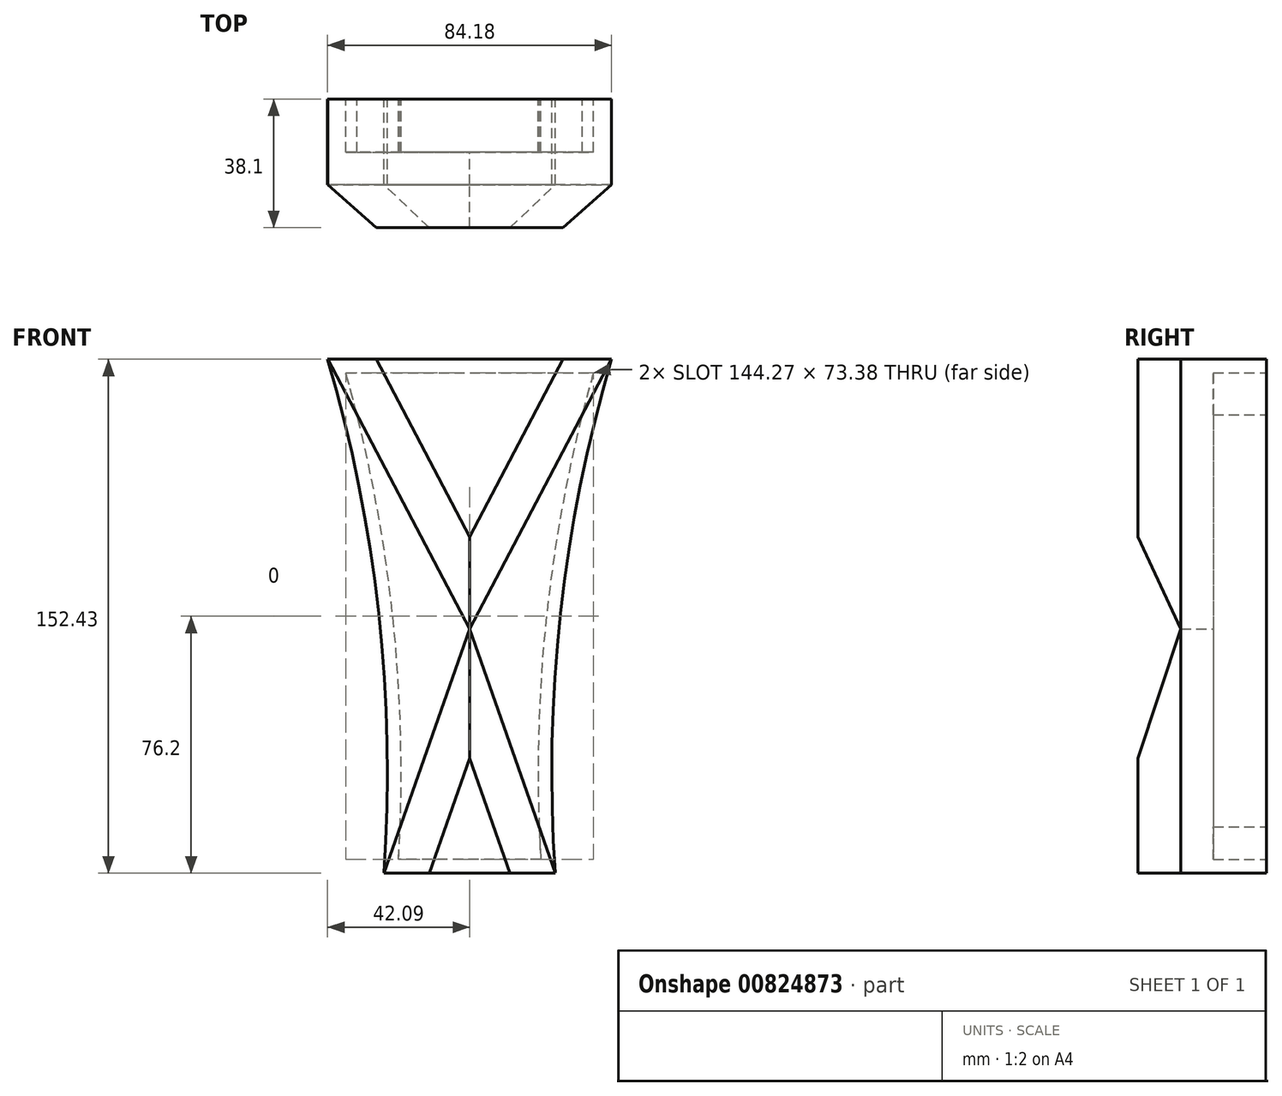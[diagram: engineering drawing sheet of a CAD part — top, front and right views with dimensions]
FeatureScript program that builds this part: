
annotation { "Feature Type Name" : "Feature", "Feature Type Description" : "" }
export const myFeature = defineFeature(function(context is Context, id is Id, definition is map)
    precondition{}
    {
        {
            var Q0;
            Q0=qCreatedBy(makeId("Front.planeOp"),FACE);
            var sketch = newSketch(context, id + "F0", { "sketchPlane" : qUnion([Q0])});
            skLineSegment(sketch, "E0", {"start": v(0, 0) * mm, "end": v(25.4, 0) * mm});
            skLineSegment(sketch, "E1", {"start": v(0, 152.4) * mm, "end": v(42.1, 152.4) * mm});
            skArc(sketch, "E2", {"start": v(42.1, 152.4) * mm, "mid": v(26.94, 76.95) * mm, "end": v(25.4, 0) * mm});
            skLineSegment(sketch, "E3", {"start": v(0, 158.6) * mm, "end": v(0, -10.52) * mm, "construction": true});
            skLineSegment(sketch, "E4.MirrorCS", {"start": v(0, 152.4) * mm, "end": v(-42.1, 152.4) * mm});
            skArc(sketch, "E5.MirrorCS", {"start": v(-42.1, 152.4) * mm, "mid": v(-26.94, 76.95) * mm, "end": v(-25.4, 0) * mm});
            skLineSegment(sketch, "E6.MirrorCS", {"start": v(0, 0) * mm, "end": v(-25.4, 0) * mm});
            skSolve(sketch);
        }
        {
            var Q0;
            Q0=qCreatedBy(makeId("Front.planeOp"),FACE);
            var sketch = newSketch(context, id + "F1", { "sketchPlane" : qUnion([Q0])});
            skLineSegment(sketch, "E7", {"start": v(-42.07, 152.43) * mm, "end": v(0, 72.46) * mm});
            skLineSegment(sketch, "E8", {"start": v(0, 72.46) * mm, "end": v(-25.43, 0) * mm});
            skLineSegment(sketch, "E9.MirrorCS", {"start": v(42.07, 152.43) * mm, "end": v(0, 72.46) * mm});
            skLineSegment(sketch, "E10.MirrorCS", {"start": v(0, 72.46) * mm, "end": v(25.43, 0) * mm});
            skLineSegment(sketch, "E11", {"start": v(-42.07, 152.43) * mm, "end": v(42.07, 152.43) * mm});
            skLineSegment(sketch, "E12", {"start": v(-25.43, 0) * mm, "end": v(25.43, 0) * mm});
            skSolve(sketch);
        }
        {
            var Q0;
            Q0=makeQuery(id+"F0.imprint","IMPRINT",FACE,{"disambiguationData":[TD([[makeQuery(id+"F0.imprint","IMPRINT",EDGE,{"derivedFrom":sQuery(id+"F0.wireOp",EDGE,"E0")}),1.0]])]});
            var Q1;
            Q1=sQuery(id+"F0.wireOp",EDGE,"E2");
            extrude(context, id + "F2", {"entities" : qUnion([Q0]), "surfaceEntities" : qUnion([Q1]), "depth" : 25.4 * mm, "offsetDistance" : 25.4 * mm});
        }
        {
            var Q0;
            Q0 = qSketchRegion(id + "F1", true);
            extrude(context, id + "F3", {"entities" : qUnion([Q0]), "depth" : 38.1 * mm, "offsetDistance" : 25.4 * mm});
        }
        {
            var Q0;
            Q0=makeQuery(id+"F3.opExtrude","CAP_EDGE",EDGE,{"disambiguationData":[OSD([sQuery(id+"F1.wireOp",EDGE,"E7")])],"isStart":false});
            var Q1;
            Q1=makeQuery(id+"F3.opExtrude","CAP_EDGE",EDGE,{"disambiguationData":[OSD([sQuery(id+"F1.wireOp",EDGE,"E8")])],"isStart":false});
            var Q2;
            Q2=makeQuery(id+"F3.opExtrude","CAP_EDGE",EDGE,{"disambiguationData":[OSD([sQuery(id+"F1.wireOp",EDGE,"E10.MirrorCS")])],"isStart":false});
            var Q3;
            Q3=makeQuery(id+"F3.opExtrude","CAP_EDGE",EDGE,{"disambiguationData":[OSD([sQuery(id+"F1.wireOp",EDGE,"E9.MirrorCS")])],"isStart":false});
            chamfer(context, id + "F4", {"entities" : qUnion([Q0, Q1, Q2, Q3]), "width" : 12.7 * mm, "tangentPropagation" : true});
        }
        {
            var Q0;
            Q0=makeQuery(id+"F0.imprint","IMPRINT",FACE,{"disambiguationData":[TD([[makeQuery(id+"F0.imprint","IMPRINT",EDGE,{"derivedFrom":sQuery(id+"F0.wireOp",EDGE,"E0")}),1.0]])]});
            var sketch = newSketch(context, id + "F5", { "sketchPlane" : qUnion([Q0])});
            skLineSegment(sketch, "E13.0", {"start": v(0, 148.34) * mm, "end": v(36.69, 148.34) * mm});
            skLineSegment(sketch, "E13.1", {"start": v(0, 4.06) * mm, "end": v(21.07, 4.06) * mm});
            skLineSegment(sketch, "E13.2", {"start": v(0, 4.06) * mm, "end": v(-21.07, 4.06) * mm});
            skArc(sketch, "E13.3", {"start": v(36.69, 148.34) * mm, "mid": v(22.84, 76.85) * mm, "end": v(21.07, 4.06) * mm});
            skArc(sketch, "E13.4", {"start": v(-36.69, 148.34) * mm, "mid": v(-22.84, 76.85) * mm, "end": v(-21.07, 4.06) * mm});
            skLineSegment(sketch, "E13.5", {"start": v(0, 148.34) * mm, "end": v(-36.69, 148.34) * mm});
            skSolve(sketch);
        }
        {
            var Q0;
            Q0=makeQuery(id+"F5.imprint","IMPRINT",FACE,{"disambiguationData":[TD([[makeQuery(id+"F5.imprint","IMPRINT",EDGE,{"derivedFrom":sQuery(id+"F5.wireOp",EDGE,"E13.0")}),-1.0]])]});
            extrude(context, id + "F6", {"entities" : qUnion([Q0]), "operationType" : NewBodyOperationType.REMOVE, "depth" : 15.75 * mm, "offsetDistance" : 25.4 * mm});
        }
    });
